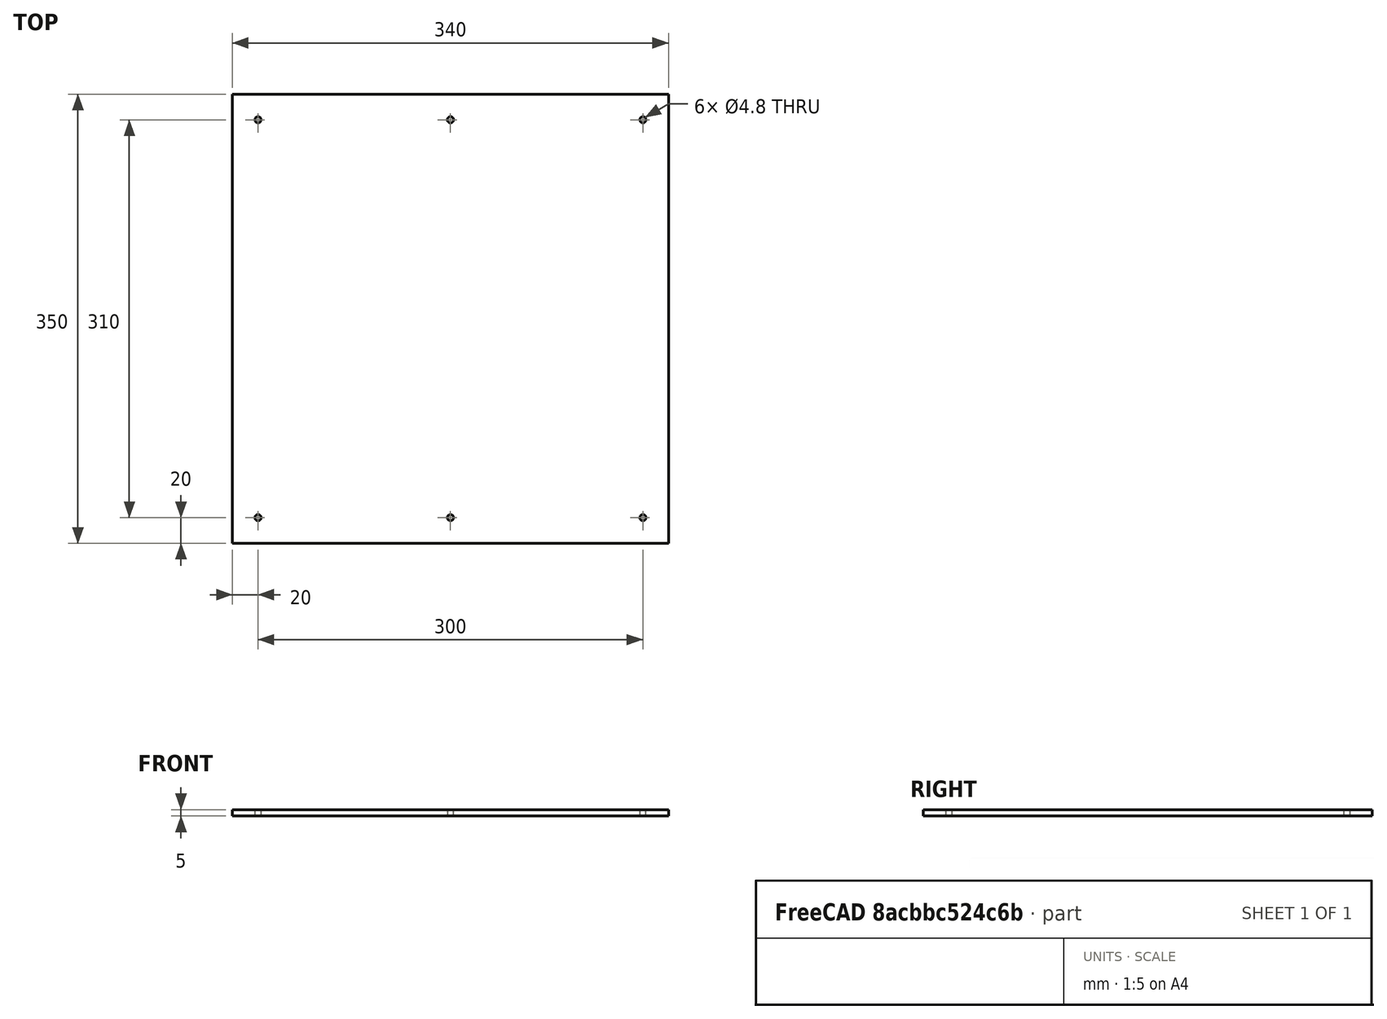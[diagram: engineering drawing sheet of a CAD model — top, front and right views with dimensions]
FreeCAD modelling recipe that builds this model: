
FCSTD DOCUMENT  (FreeCAD 0.16R6703 (Git))
Label: bed-plate
License: All rights reserved
LicenseURL: http://de.wikipedia.org/wiki/Alle_Rechte_vorbehalten
objects: Sketcher::SketchObject×1, PartDesign::Pad×1
note: 3 computed .brp shape members not serialized (recipe doc carries the construction recipe); baked Part::Feature solids carry a one-line shape summary decoded from their .brp

FEATURE [Sketcher::SketchObject] Sketch
  sketch-geometry (38):
    g0: LineSegment StartX=-170 StartY=175 StartZ=0 EndX=170 EndY=175 EndZ=0
    g1: LineSegment StartX=170 StartY=175 StartZ=0 EndX=170 EndY=-175 EndZ=0
    g2: LineSegment StartX=170 StartY=-175 StartZ=0 EndX=-170 EndY=-175 EndZ=0
    g3: LineSegment StartX=-170 StartY=-175 StartZ=0 EndX=-170 EndY=175 EndZ=0
    g4: Circle CenterX=-150 CenterY=155 CenterZ=0 NormalX=0 NormalY=0 NormalZ=1 Radius=2.4
    g5: Circle CenterX=150 CenterY=155 CenterZ=0 NormalX=0 NormalY=0 NormalZ=1 Radius=2.4
    g6: Circle CenterX=150 CenterY=-155 CenterZ=0 NormalX=0 NormalY=0 NormalZ=1 Radius=2.4
    g7: Circle CenterX=-150 CenterY=-155 CenterZ=0 NormalX=0 NormalY=0 NormalZ=1 Radius=2.4
    g8: Circle CenterX=0 CenterY=-155 CenterZ=0 NormalX=0 NormalY=0 NormalZ=1 Radius=2.4
    g9: Circle CenterX=0 CenterY=155 CenterZ=0 NormalX=0 NormalY=0 NormalZ=1 Radius=2.4
    g10: LineSegment [constr] StartX=-150 StartY=155 StartZ=0 EndX=150 EndY=155 EndZ=0
    g11: LineSegment [constr] StartX=150 StartY=155 StartZ=0 EndX=150 EndY=-155 EndZ=0
    g12: LineSegment [constr] StartX=150 StartY=-155 StartZ=0 EndX=-150 EndY=-155 EndZ=0
    g13: LineSegment [constr] StartX=-150 StartY=-155 StartZ=0 EndX=-150 EndY=155 EndZ=0
    g14: LineSegment [constr] StartX=-130 StartY=125 StartZ=0 EndX=-130 EndY=20 EndZ=0
    g15: LineSegment [constr] StartX=-130 StartY=20 StartZ=0 EndX=-30 EndY=20 EndZ=0
    g16: LineSegment [constr] StartX=-30 StartY=20 StartZ=0 EndX=-130 EndY=125 EndZ=0
    g17: LineSegment [constr] StartX=-117.5 StartY=135 StartZ=0 EndX=-17.5 EndY=30 EndZ=0
    g18: LineSegment [constr] StartX=-17.5 StartY=30 StartZ=0 EndX=-17.5 EndY=135 EndZ=0
    g19: LineSegment [constr] StartX=-17.5 StartY=135 StartZ=0 EndX=-117.5 EndY=135 EndZ=0
    g20: LineSegment [constr] StartX=17.5 StartY=135 StartZ=0 EndX=17.5 EndY=30 EndZ=0
    g21: LineSegment [constr] StartX=17.5 StartY=30 StartZ=0 EndX=130 EndY=135 EndZ=0
    g22: LineSegment [constr] StartX=130 StartY=135 StartZ=0 EndX=17.5 EndY=135 EndZ=0
    g23: LineSegment [constr] StartX=142.5 StartY=125 StartZ=0 EndX=142.5 EndY=20 EndZ=0
    g24: LineSegment [constr] StartX=142.5 StartY=20 StartZ=0 EndX=30 EndY=20 EndZ=0
    g25: LineSegment [constr] StartX=30 StartY=20 StartZ=0 EndX=142.5 EndY=125 EndZ=0
    g26: LineSegment [constr] StartX=30 StartY=-20 StartZ=0 EndX=142.5 EndY=-125 EndZ=0
    g27: LineSegment [constr] StartX=142.5 StartY=-125 StartZ=0 EndX=142.5 EndY=-20 EndZ=0
    g28: LineSegment [constr] StartX=142.5 StartY=-20 StartZ=0 EndX=30 EndY=-20 EndZ=0
    g29: LineSegment [constr] StartX=17.5 StartY=-30 StartZ=0 EndX=130 EndY=-135 EndZ=0
    g30: LineSegment [constr] StartX=130 StartY=-135 StartZ=0 EndX=17.5 EndY=-135 EndZ=0
    g31: LineSegment [constr] StartX=17.5 StartY=-135 StartZ=0 EndX=17.5 EndY=-30 EndZ=0
    g32: LineSegment [constr] StartX=-130 StartY=-20 StartZ=0 EndX=-130 EndY=-125 EndZ=0
    g33: LineSegment [constr] StartX=-130 StartY=-125 StartZ=0 EndX=-30 EndY=-20 EndZ=0
    g34: LineSegment [constr] StartX=-30 StartY=-20 StartZ=0 EndX=-130 EndY=-20 EndZ=0
    g35: LineSegment [constr] StartX=-17.5 StartY=-30 StartZ=0 EndX=-117.5 EndY=-135 EndZ=0
    g36: LineSegment [constr] StartX=-117.5 StartY=-135 StartZ=0 EndX=-17.5 EndY=-135 EndZ=0
    g37: LineSegment [constr] StartX=-17.5 StartY=-135 StartZ=0 EndX=-17.5 EndY=-30 EndZ=0
  constraints (108):
    c: Coincident(g0,g1)
    c: Coincident(g1,g2)
    c: Coincident(g2,g3)
    c: Coincident(g3,g0)
    c: Horizontal(g0)
    c: Horizontal(g2)
    c: Vertical(g1)
    c: Vertical(g3)
    c: Symmetric(g0,g0,g-2)
    c: Symmetric(g1,g0,g-1)
    c: DistanceX(g0,g0) = 340
    c: DistanceY(g1,g1) = 350
    c: Equal(g4,g9)
    c: Equal(g9,g5)
    c: Equal(g5,g6)
    c: Equal(g6,g8)
    c: Equal(g8,g7)
    c: Coincident(g10,g11)
    c: Coincident(g11,g12)
    c: Coincident(g12,g13)
    c: Coincident(g13,g10)
    c: Horizontal(g10)
    c: Horizontal(g12)
    c: Vertical(g11)
    c: Vertical(g13)
    c: Coincident(g10,g4)
    c: Coincident(g11,g6)
    c: PointOnObject(g8,g12)
    c: Coincident(g7,g12)
    c: PointOnObject(g8,g-2)
    c: PointOnObject(g9,g10)
    c: PointOnObject(g9,g-2)
    c: Coincident(g5,g10)
    c: DistanceX(g10,g10) = 300
    c: Symmetric(g5,g4,g-2)
    c: Symmetric(g5,g6,g-1)
    c: DistanceY(g11,g11) = 310
    c: Vertical(g14)
    c: Coincident(g14,g15)
    c: Horizontal(g15)
    c: Coincident(g15,g16)
    c: Coincident(g16,g14)
    c: Coincident(g17,g18)
    c: Vertical(g18)
    c: Coincident(g18,g19)
    c: Coincident(g19,g17)
    c: Vertical(g20)
    c: Coincident(g20,g21)
    c: Coincident(g21,g22)
    c: Coincident(g22,g20)
    c: Vertical(g23)
    c: Coincident(g23,g24)
    c: Horizontal(g24)
    c: Coincident(g24,g25)
    c: Coincident(g25,g23)
    c: Coincident(g26,g27)
    c: Vertical(g27)
    c: Coincident(g27,g28)
    c: Coincident(g28,g26)
    c: Coincident(g29,g30)
    c: Horizontal(g30)
    c: Coincident(g30,g31)
    c: Coincident(g31,g29)
    c: Vertical(g32)
    c: Coincident(g32,g33)
    c: Coincident(g33,g34)
    c: Coincident(g34,g32)
    c: Coincident(g35,g36)
    c: Coincident(g36,g37)
    c: Coincident(g37,g35)
    c: Vertical(g37)
    c: Horizontal(g34)
    c: Vertical(g31)
    c: Equal(g14,g18)
    c: Parallel(g16,g17)
    c: Equal(g15,g19)
    c: Equal(g34,g15)
    c: Equal(g32,g37)
    c: Parallel(g35,g33)
    c: Horizontal(g36)
    c: Equal(g36,g34)
    c: Equal(g31,g37)
    c: Equal(g30,g28)
    c: Horizontal(g28)
    c: Equal(g31,g27)
    c: Parallel(g21,g25)
    c: Equal(g24,g28)
    c: Horizontal(g22)
    c: Equal(g20,g23)
    c: Equal(g24,g22)
    c: Equal(g16,g17)
    c: Symmetric(g35,g29,g-2)
    c: Symmetric(g33,g26,g-2)
    c: Symmetric(g15,g24,g-2)
    c: Symmetric(g20,g17,g-2)
    c: Symmetric(g26,g24,g-1)
    c: Symmetric(g29,g20,g-1)
    c: Symmetric(g14,g32,g-1)
    c: Equal(g20,g18)
    c: DistanceX(g36,g36) = 100
    c: DistanceY(g32,g14) = 40
    c: DistanceX(g36,g30) = 35
    c: DistanceY(g6,g29) = 20
    c: DistanceX(g7,g32) = 20
    c: Equal(g18,g37)
    c: DistanceY(g23,g0) = 50
    c: DistanceX(g29,g1) = 40
    c: Radius(g7) = 2.4
FEATURE [PartDesign::Pad] Pad
  Length = 5
  Length2 = 100
  Sketch = -> Sketch
  Type = 0
